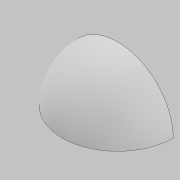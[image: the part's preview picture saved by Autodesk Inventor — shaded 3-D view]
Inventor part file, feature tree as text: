
AUTODESK INVENTOR PART (.ipt)
format: ipt  version: 2021 (Build 250183000, 183)  size: 122,880 bytes
history: native  units: mm
features: other x2, revolve x1, sketch x1
ambient origin geometry x8: Origin, YZ Plane, XZ Plane, XY Plane, X Axis, Y Axis, Z Axis, Center Point
bodies: Body1 (feature_tree)
feature tree (4):
  revolve  "Revolution1"  [1 undecoded]
  other  "tangent1"
  other  "tangent2"
  sketch  "Sketch1"  dims[d0=10.0mm d1=900.0mm d2=0.0mm d3=0.0mm d6=180.0deg d7=900.0mm d8=-900.0mm]
note: 1 required parameter value undecoded (feature->parameter linkage not recoverable at this tier; creation-order binding heuristic only, values carry confidence <= 0.55)
